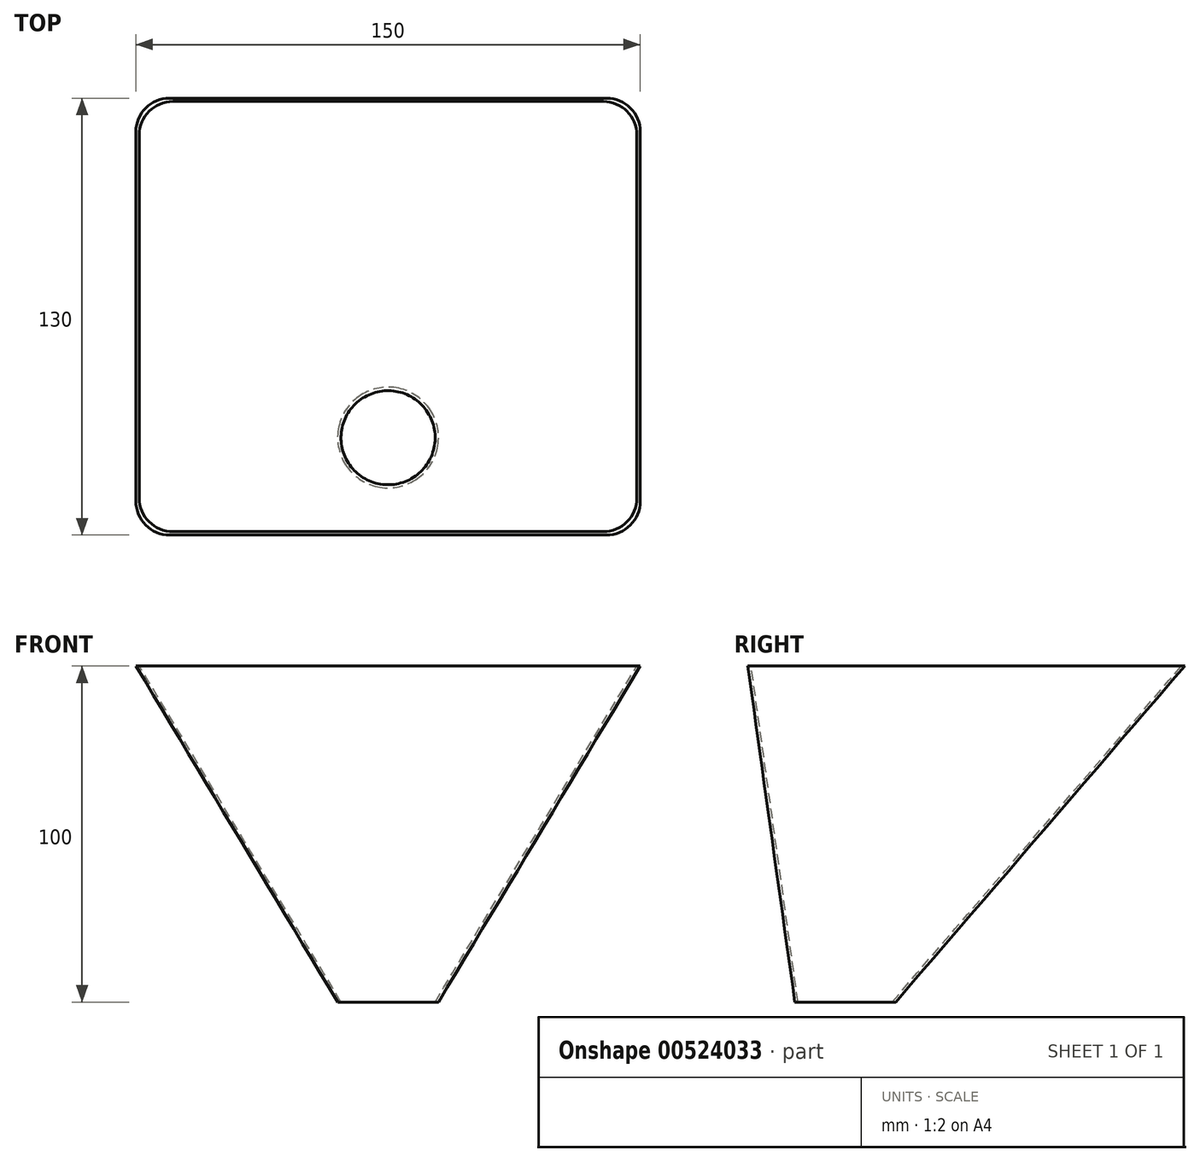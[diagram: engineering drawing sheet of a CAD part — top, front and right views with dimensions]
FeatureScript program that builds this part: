
annotation { "Feature Type Name" : "Feature", "Feature Type Description" : "" }
export const myFeature = defineFeature(function(context is Context, id is Id, definition is map)
    precondition{}
    {
        {
            var Q0;
            Q0=qCreatedBy(makeId("Top.planeOp"),FACE);
            var sketch = newSketch(context, id + "F0", { "sketchPlane" : qUnion([Q0])});
            skLineSegment(sketch, "E0.bottom", {"start": v(-65, 65) * mm, "end": v(65, 65) * mm});
            skLineSegment(sketch, "E0.top", {"start": v(-65, -65) * mm, "end": v(65, -65) * mm});
            skLineSegment(sketch, "E0.left", {"start": v(-75, 55) * mm, "end": v(-75, -55) * mm});
            skLineSegment(sketch, "E0.right", {"start": v(75, 55) * mm, "end": v(75, -55) * mm});
            skPoint(sketch, "E0.middle", {"position": v(0, 0) * mm});
            skPoint(sketch, "E1.visualSharp", {"position": v(-75, 65) * mm});
            skArc(sketch, "E1.filletArc", {"start": v(-65, 65) * mm, "mid": v(-72.07, 62.07) * mm, "end": v(-75, 55) * mm});
            skPoint(sketch, "E2.visualSharp", {"position": v(75, 65) * mm});
            skArc(sketch, "E2.filletArc", {"start": v(75, 55) * mm, "mid": v(72.07, 62.07) * mm, "end": v(65, 65) * mm});
            skPoint(sketch, "E3.visualSharp", {"position": v(75, -65) * mm});
            skArc(sketch, "E3.filletArc", {"start": v(65, -65) * mm, "mid": v(72.07, -62.07) * mm, "end": v(75, -55) * mm});
            skPoint(sketch, "E4.visualSharp", {"position": v(-75, -65) * mm});
            skArc(sketch, "E4.filletArc", {"start": v(-75, -55) * mm, "mid": v(-72.07, -62.07) * mm, "end": v(-65, -65) * mm});
            skSolve(sketch);
        }
        {
            var Q0;
            Q0=qCreatedBy(makeId("Top.planeOp"),FACE);
            var sketch = newSketch(context, id + "F1", { "sketchPlane" : qUnion([Q0])});
            skLineSegment(sketch, "E5.bottom", {"start": v(-64, 64) * mm, "end": v(64, 64) * mm});
            skLineSegment(sketch, "E5.top", {"start": v(-64, -64) * mm, "end": v(64, -64) * mm});
            skLineSegment(sketch, "E5.left", {"start": v(-74, 54) * mm, "end": v(-74, -54) * mm});
            skLineSegment(sketch, "E5.right", {"start": v(74, 54) * mm, "end": v(74, -54) * mm});
            skPoint(sketch, "E5.middle", {"position": v(0, 0) * mm});
            skPoint(sketch, "E6.visualSharp", {"position": v(-74, 64) * mm});
            skArc(sketch, "E6.filletArc", {"start": v(-64, 64) * mm, "mid": v(-71.07, 61.07) * mm, "end": v(-74, 54) * mm});
            skPoint(sketch, "E7.visualSharp", {"position": v(74, 64) * mm});
            skArc(sketch, "E7.filletArc", {"start": v(74, 54) * mm, "mid": v(71.07, 61.07) * mm, "end": v(64, 64) * mm});
            skPoint(sketch, "E8.visualSharp", {"position": v(74, -64) * mm});
            skArc(sketch, "E8.filletArc", {"start": v(64, -64) * mm, "mid": v(71.07, -61.07) * mm, "end": v(74, -54) * mm});
            skPoint(sketch, "E9.visualSharp", {"position": v(-74, -64) * mm});
            skArc(sketch, "E9.filletArc", {"start": v(-74, -54) * mm, "mid": v(-71.07, -61.07) * mm, "end": v(-64, -64) * mm});
            skSolve(sketch);
        }
        {
            var Q0;
            Q0=qCreatedBy(makeId("Top.planeOp"),FACE);
            cPlane(context, id + "F2", {"entities" : qUnion([Q0]), "cplaneType" : CPlaneType.OFFSET, "offset" : 100 * mm, "oppositeDirection" : true, "width" : 150 * mm, "height" : 150 * mm});
        }
        {
            var Q0;
            Q0=qCreatedBy(id+"F2.planeOp",FACE);
            var sketch = newSketch(context, id + "F3", { "sketchPlane" : qUnion([Q0])});
            skCircle(sketch, "E10", {"center": v(0, -36) * mm, "radius": 15 * mm});
            skSolve(sketch);
        }
        {
            var Q0;
            Q0=qCreatedBy(id+"F2.planeOp",FACE);
            var sketch = newSketch(context, id + "F4", { "sketchPlane" : qUnion([Q0])});
            skCircle(sketch, "E11", {"center": v(0, -36.06) * mm, "radius": 14 * mm});
            skSolve(sketch);
        }
        {
            var Q0;
            Q0 = qSketchRegion(id + "F0", true);
            var Q1;
            Q1 = qSketchRegion(id + "F3", true);
            loft(context, id + "F5", {"sheetProfilesArray" : [{ "sheetProfileEntities" : qUnion([Q0]) }, { "sheetProfileEntities" : qUnion([Q1]) }]});
        }
        {
            var Q1;
            Q1 = qSketchRegion(id + "F1", true);
            var Q2;
            Q2 = qSketchRegion(id + "F4", true);
            loft(context, id + "F6", {"operationType" : NewBodyOperationType.REMOVE, "sheetProfilesArray" : [{ "sheetProfileEntities" : qUnion([Q1]) }, { "sheetProfileEntities" : qUnion([Q2]) }]});
        }
    });
